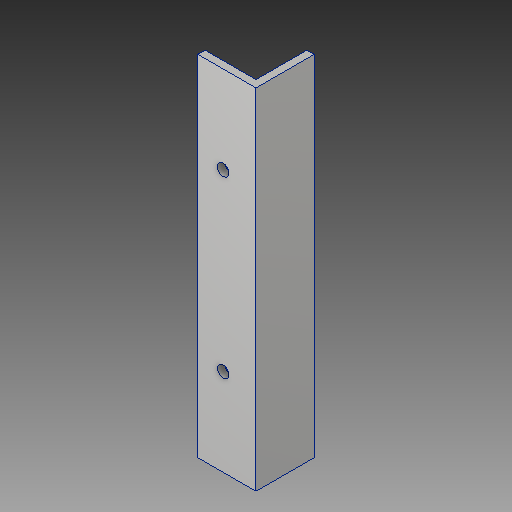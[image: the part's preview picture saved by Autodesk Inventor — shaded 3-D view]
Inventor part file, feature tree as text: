
AUTODESK INVENTOR PART (.ipt)
format: ipt  version: 2018 (Build 220112000, 112)  size: 112,640 bytes
history: native  units: in
note: dims shown in document units (in); Inventor stores cm internally (conversion verified against a paired STEP export)
features: sketch x3, extrude x2
ambient origin geometry x8: Origin, YZ Plane, XZ Plane, XY Plane, X Axis, Y Axis, Z Axis, Center Point
bodies: Solid1 (feature_tree)
feature tree (5):
  extrude  "Extrusion1"  Depth=0.125in
  sketch  "Sketch2"  dims[d2=1.0in d3=0.125in]
  extrude  "Extrusion2"  Depth=0.125in
  sketch  "Sketch1"  dims[d0=1.0in d1=0.125in]
  sketch  "Sketch3"  dims[d4=6.0in d5=0.0in d6=1.5in d7=3.0in d8=0.2in d9=1.0in d10=0.0in]
